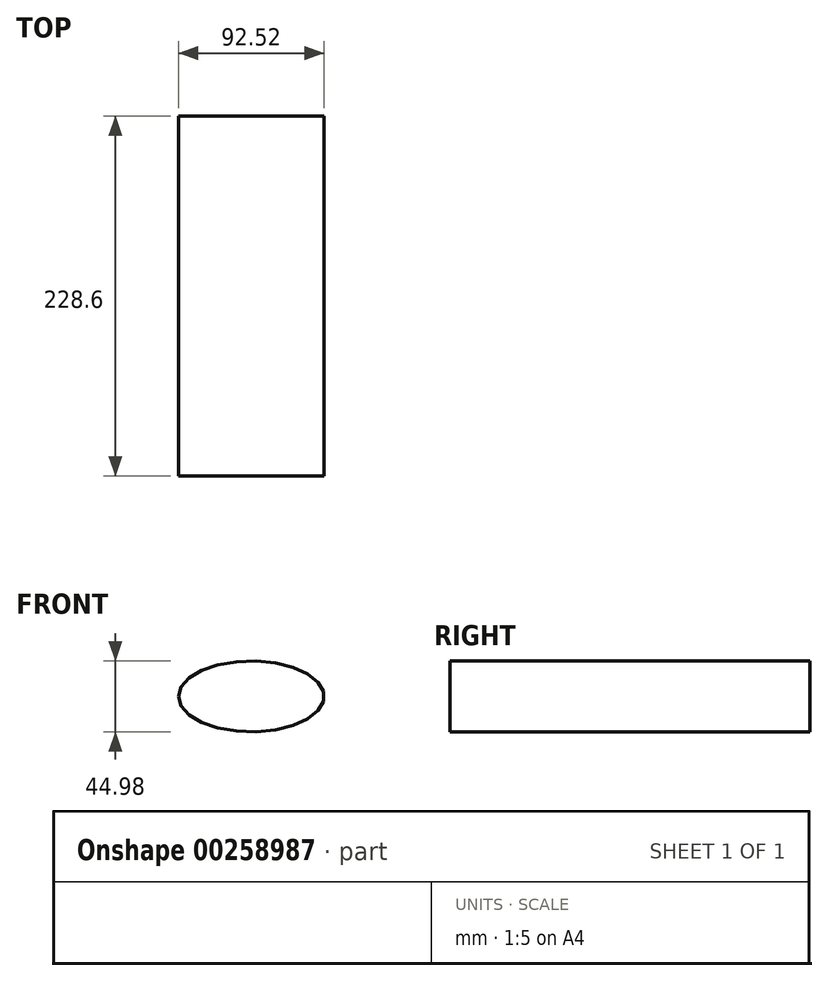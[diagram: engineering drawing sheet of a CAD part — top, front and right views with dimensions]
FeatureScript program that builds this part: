
annotation { "Feature Type Name" : "Feature", "Feature Type Description" : "" }
export const myFeature = defineFeature(function(context is Context, id is Id, definition is map)
    precondition{}
    {
        {
            var Q0;
            Q0=qCreatedBy(makeId("Front.planeOp"),FACE);
            var sketch = newSketch(context, id + "F0", { "sketchPlane" : qUnion([Q0])});
            skEllipse(sketch, "E0", {"center": v(0, 0) * mm, "majorRadius": 46.26 * mm, "minorRadius": 22.5 * mm, "majorAxis": v(-1, 0)});
            skSolve(sketch);
        }
        {
            var Q0;
            Q0 = qSketchRegion(id + "F0", true);
            var Q1;
            Q1=makeQuery(id+"F0.imprint","IMPRINT",FACE,{"disambiguationData":[TD([[makeQuery(id+"F0.imprint","IMPRINT",EDGE,{"derivedFrom":sQuery(id+"F0.wireOp",EDGE,"E0")}),1.0]])]});
            extrude(context, id + "F1", {"entities" : qUnion([Q0, Q1]), "depth" : 228.6 * mm});
        }
    });
